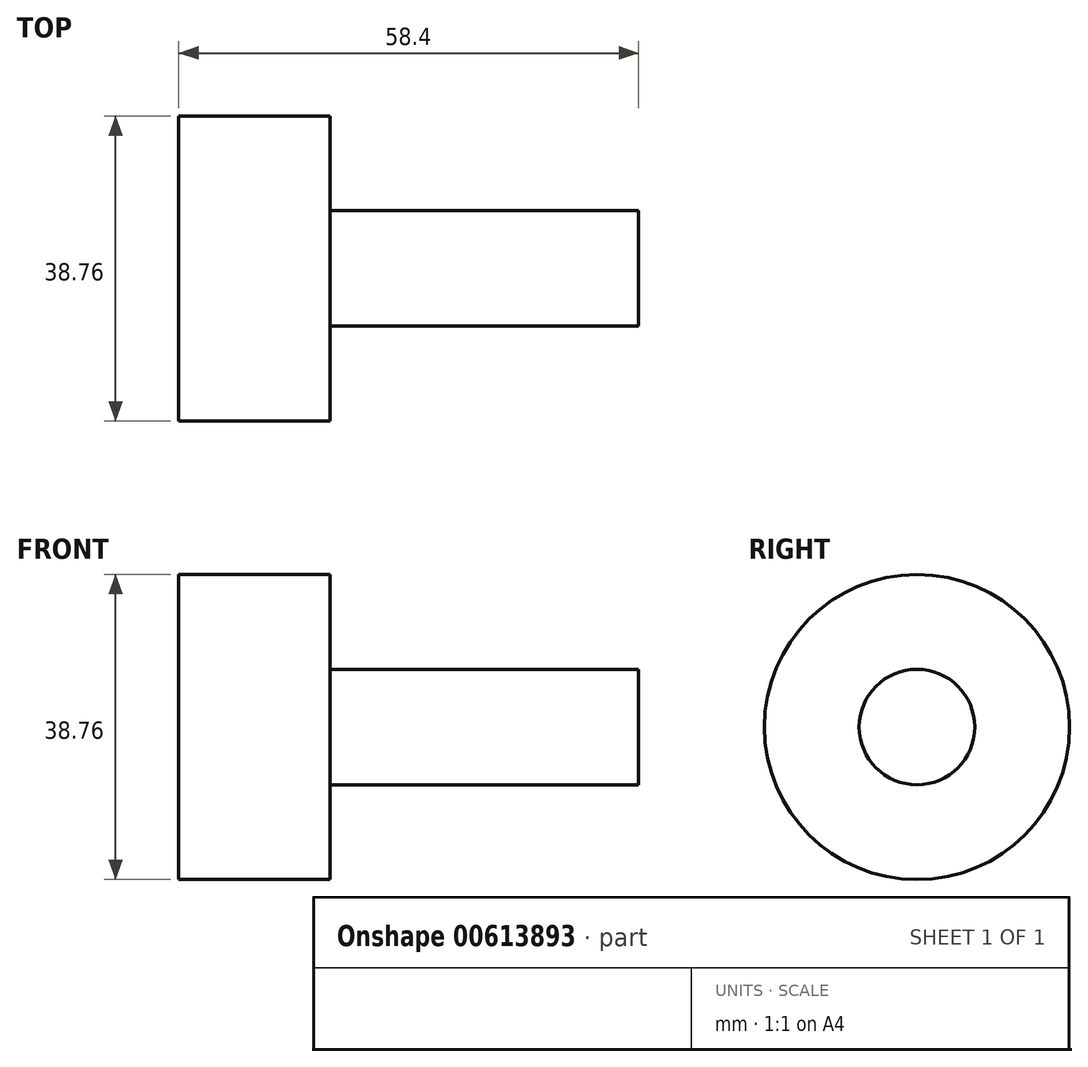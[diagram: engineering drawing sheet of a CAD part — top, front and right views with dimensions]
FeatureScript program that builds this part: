
annotation { "Feature Type Name" : "Feature", "Feature Type Description" : "" }
export const myFeature = defineFeature(function(context is Context, id is Id, definition is map)
    precondition{}
    {
        {
            var Q0;
            Q0=qCreatedBy(makeId("Front.planeOp"),FACE);
            var sketch = newSketch(context, id + "F0", { "sketchPlane" : qUnion([Q0])});
            skLineSegment(sketch, "E0.bottom", {"start": v(-68.05, 33.68) * mm, "end": v(-48.84, 33.68) * mm});
            skLineSegment(sketch, "E0.left", {"start": v(-68.05, 33.68) * mm, "end": v(-68.05, 14.3) * mm});
            skLineSegment(sketch, "E0.right", {"start": v(-48.84, 33.68) * mm, "end": v(-48.84, 14.3) * mm});
            skPoint(sketch, "E1.top.end.orphan", {"position": v(0, 4) * mm});
            skLineSegment(sketch, "E2.bottom", {"start": v(-48.84, 21.64) * mm, "end": v(-9.65, 21.64) * mm});
            skLineSegment(sketch, "E2.left", {"start": v(-48.84, 21.64) * mm, "end": v(-48.84, 14.3) * mm});
            skLineSegment(sketch, "E2.right", {"start": v(-9.65, 21.64) * mm, "end": v(-9.65, 14.3) * mm});
            skLineSegment(sketch, "E3", {"start": v(-73.36, 14.3) * mm, "end": v(-3.2, 14.3) * mm});
            skPoint(sketch, "E3.startSnap0", {"position": v(-68.05, 14.3) * mm});
            skPoint(sketch, "E0.top.start.orphan", {"position": v(-68.05, -5.08) * mm});
            skSolve(sketch);
        }
        {
            var Q0;
            Q0 = qSketchRegion(id + "F0", true);
            var Q1;
            Q1=sQuery(id+"F0.wireOp",EDGE,"E3");
            revolve(context, id + "F1", {"entities" : qUnion([Q0]), "axis" : qUnion([Q1]), "revolveType" : RevolveType.FULL});
        }
    });
